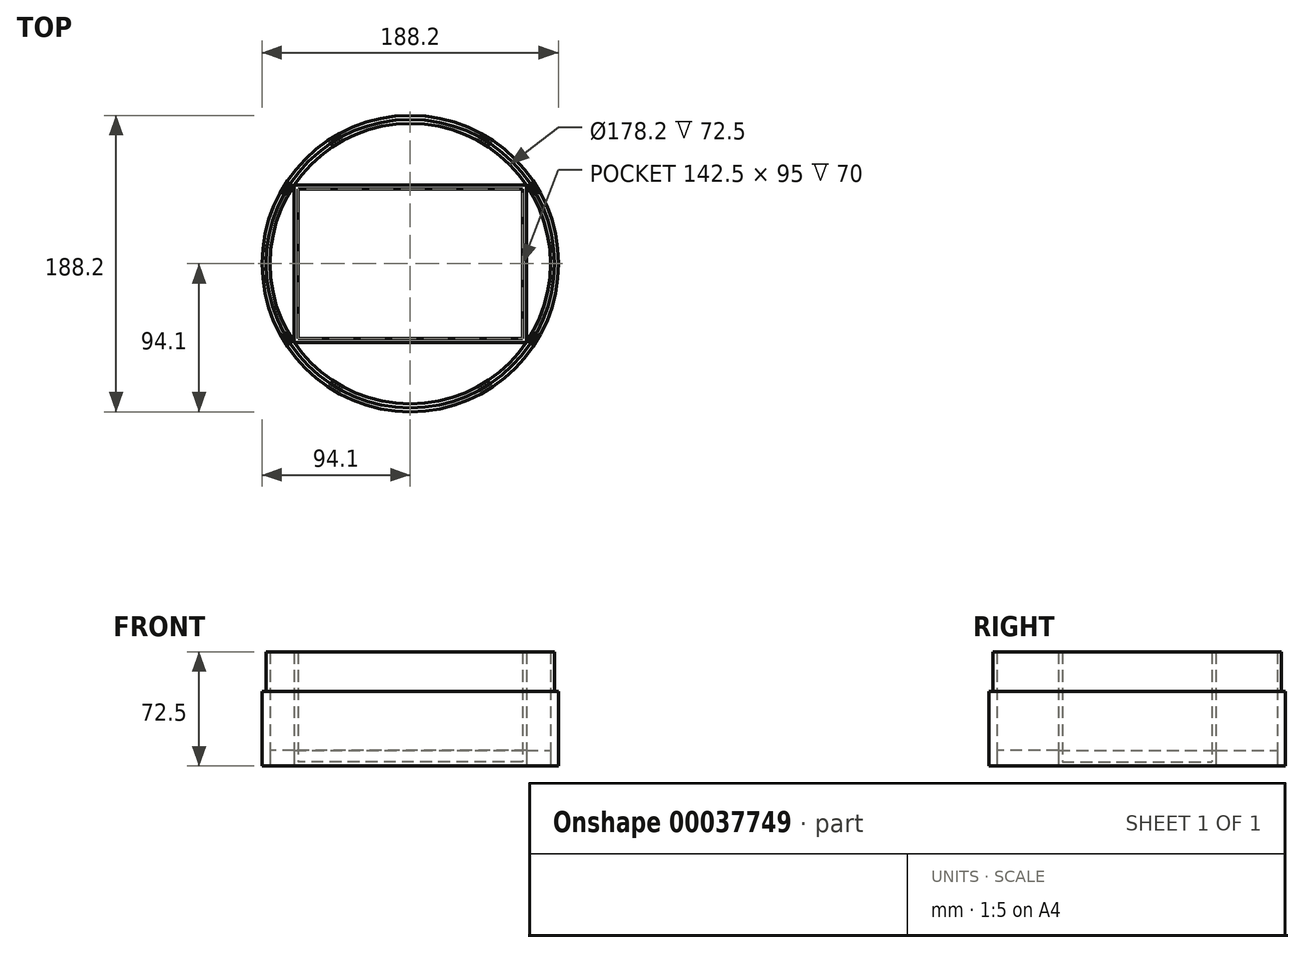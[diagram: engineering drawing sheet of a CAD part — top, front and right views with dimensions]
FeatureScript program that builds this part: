
annotation { "Feature Type Name" : "Feature", "Feature Type Description" : "" }
export const myFeature = defineFeature(function(context is Context, id is Id, definition is map)
    precondition{}
    {
        {
            var Q0;
            Q0=qCreatedBy(makeId("Top.planeOp"),FACE);
            var sketch = newSketch(context, id + "F0", { "sketchPlane" : qUnion([Q0])});
            skLineSegment(sketch, "E0.rect.bottom", {"start": v(73.75, -50) * mm, "end": v(-73.75, -50) * mm});
            skLineSegment(sketch, "E0.rect.top", {"start": v(73.75, 50) * mm, "end": v(-73.75, 50) * mm});
            skLineSegment(sketch, "E0.rect.left", {"start": v(73.75, -50) * mm, "end": v(73.75, 50) * mm});
            skLineSegment(sketch, "E0.rect.right", {"start": v(-73.75, -50) * mm, "end": v(-73.75, 50) * mm});
            skPoint(sketch, "E0.rect.middle", {"position": v(0, 0) * mm});
            skLineSegment(sketch, "E1", {"start": v(0, 0) * mm, "end": v(0, -50) * mm, "construction": true});
            skLineSegment(sketch, "E2", {"start": v(0, -50) * mm, "end": v(0, 50) * mm, "construction": true});
            skLineSegment(sketch, "E3", {"start": v(-1.25, -50) * mm, "end": v(-1.25, 50) * mm});
            skLineSegment(sketch, "E4.MirrorCS", {"start": v(1.25, -50) * mm, "end": v(1.25, 50) * mm});
            skCircle(sketch, "E5", {"center": v(0, 0) * mm, "radius": 89.1 * mm});
            skCircle(sketch, "E6", {"center": v(0, 0) * mm, "radius": 94.1 * mm});
            skLineSegment(sketch, "E7", {"start": v(-93.97, -4.99) * mm, "end": v(94.1, 0) * mm, "construction": true});
            skPoint(sketch, "E7.endSnap0", {"position": v(1.25, 0) * mm});
            skSolve(sketch);
        }
        {
            var Q0;
            Q0 = qSketchRegion(id + "F0", true);
            var Q1;
            {var subQ1=sQuery(id+"F0.wireOp",EDGE,"E0.rect.right");Q1=makeQuery(id+"F0.imprint","IMPRINT",FACE,{"disambiguationData":[TD([[makeQuery(id+"F0.imprint","IMPRINT",EDGE,{"derivedFrom":subQ1}),-1.0]])]});}
            var Q2;
            {var subQ1=sQuery(id+"F0.wireOp",EDGE,"E0.rect.left");Q2=makeQuery(id+"F0.imprint","IMPRINT",FACE,{"disambiguationData":[TD([[makeQuery(id+"F0.imprint","IMPRINT",EDGE,{"derivedFrom":subQ1}),1.0]])]});}
            var Q3;
            {var subQ1=sQuery(id+"F0.wireOp",EDGE,"E3");Q3=makeQuery(id+"F0.imprint","IMPRINT",FACE,{"disambiguationData":[TD([[makeQuery(id+"F0.imprint","IMPRINT",EDGE,{"derivedFrom":subQ1}),-1.0]])]});}
            extrude(context, id + "F1", {"entities" : qUnion([Q0, Q1, Q2, Q3]), "depth" : 72.5 * mm});
        }
        {
            var Q0;
            Q0=makeQuery(id+"F1.opExtrude","CAP_FACE",FACE,{"disambiguationData":[OSD([sQuery(id+"F0.wireOp",EDGE,"E0.rect.bottom"),sQuery(id+"F0.wireOp",EDGE,"E0.rect.top"),sQuery(id+"F0.wireOp",EDGE,"E0.rect.left"),sQuery(id+"F0.wireOp",EDGE,"E0.rect.right")])],"isStart":false});
            shell(context, id + "F2", {"entities" : qUnion([Q0]), "thickness" : 2.5 * mm});
        }
        {
            var Q0;
            Q0=sQuery(id+"F0.wireOp",EDGE,"E3");
            var Q1;
            Q1=sQuery(id+"F0.wireOp",EDGE,"E4.MirrorCS");
            extrude(context, id + "F3", {"bodyType" : ToolBodyType.SURFACE, "surfaceEntities" : qUnion([Q0, Q1]), "depth" : 72.5 * mm});
        }
        {
            var Q0;
            {var subQ1=sQuery(id+"F0.wireOp",EDGE,"E0.rect.right");Q0=makeQuery(id+"F0.imprint","IMPRINT",FACE,{"disambiguationData":[TD([[makeQuery(id+"F0.imprint","IMPRINT",EDGE,{"derivedFrom":subQ1}),1.0]])]});}
            var Q1;
            {var subQ1=sQuery(id+"F0.wireOp",EDGE,"E0.rect.left");Q1=makeQuery(id+"F0.imprint","IMPRINT",FACE,{"disambiguationData":[TD([[makeQuery(id+"F0.imprint","IMPRINT",EDGE,{"derivedFrom":subQ1}),-1.0]])]});}
            var Q2;
            {var subQ1=sQuery(id+"F0.wireOp",EDGE,"E0.rect.top");var subQ4=makeQuery(id+"F0.imprint","INTERSECT",VERTEX,{"derivedFrom":[subQ1,sQuery(id+"F0.wireOp",EDGE,"E3")]});Q2=makeQuery(id+"F0.imprint","IMPRINT",FACE,{"disambiguationData":[TD([[makeQuery(id+"F0.imprint","IMPRINT",EDGE,{"disambiguationData":[TD([[subQ4,1.0]])],"derivedFrom":subQ1}),-1.0]])]});}
            var Q3;
            {var subQ1=sQuery(id+"F0.wireOp",EDGE,"E0.rect.bottom");var subQ4=makeQuery(id+"F0.imprint","INTERSECT",VERTEX,{"derivedFrom":[subQ1,sQuery(id+"F0.wireOp",EDGE,"E3")]});Q3=makeQuery(id+"F0.imprint","IMPRINT",FACE,{"disambiguationData":[TD([[makeQuery(id+"F0.imprint","IMPRINT",EDGE,{"disambiguationData":[TD([[subQ4,1.0]])],"derivedFrom":subQ1}),1.0]])]});}
            extrude(context, id + "F4", {"entities" : qUnion([Q0, Q1, Q2, Q3]), "depth" : 10 * mm});
        }
        {
            var Q0;
            Q0=makeQuery(id+"F1.opExtrude","CAP_FACE",FACE,{"disambiguationData":[OSD([sQuery(id+"F0.wireOp",EDGE,"E6"),sQuery(id+"F0.wireOp",EDGE,"a0b1bb28-3a9c-4cea-a828-bea117dc8ee0")])],"isStart":false});
            var sketch = newSketch(context, id + "F5", { "sketchPlane" : qUnion([Q0])});
            skCircle(sketch, "E8", {"center": v(0, 0) * mm, "radius": 91.6 * mm});
            skSolve(sketch);
        }
        {
            var Q0;
            Q0=makeQuery(id+"F5.imprint","IMPRINT",FACE,{"disambiguationData":[TD([[makeQuery(id+"F5.imprint","IMPRINT",EDGE,{"derivedFrom":sQuery(id+"F5.wireOp",EDGE,"E8")}),-1.0]])]});
            extrude(context, id + "F6", {"entities" : qUnion([Q0]), "operationType" : NewBodyOperationType.REMOVE, "oppositeDirection" : true, "depth" : 25 * mm});
        }
    });
